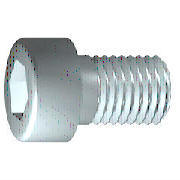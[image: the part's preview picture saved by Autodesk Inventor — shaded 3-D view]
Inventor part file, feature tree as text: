
AUTODESK INVENTOR PART (.ipt)
format: ipt  version: 2024 (Build 280153000, 153)  size: 185,856 bytes
history: native  units: mm (DEFAULTED — no unit token found)
features: fillet x2, sketch x2, extrude x1, thread x1, chamfer x1, plane x1
ambient origin geometry x7: Origin, YZ Plane, XY Plane, X Axis, Y Axis, Z Axis, Center Point
bodies: Solid1 (feature_tree), Body (feature_tree)
feature tree (8):
  extrude  "Slot"  Depth=3.0mm
  fillet  "Fillet1"  Radius=3.0mm
  thread  "Thread"  [1 undecoded]
  chamfer  "Chamfer1"  Distance=3.0mm
  plane  "Work Plane1"
  fillet  "Fillet2"  Radius=3.0mm
  sketch  "Sketch1"  dims[d1=18.0mm d2=0.306825mm d3=3.0mm d4=1.3mm]
  sketch  "Sketch2"  dims[d5=60.0deg d6=3.0mm d7=3.0mm d8=2.886751mm d9=5.5mm d10=90.0deg d11=10.0mm d12=0.0mm d13=18.0mm d14=0.0mm d15=0.306725mm d16=0.306725mm d17=0.3mm d19=0.0mm d26=25.0mm d27=45.0deg d28=0.0mm d29=0.0mm d30=0.1mm]
note: 1 required parameter value undecoded (feature->parameter linkage not recoverable at this tier; creation-order binding heuristic only, values carry confidence <= 0.55)
